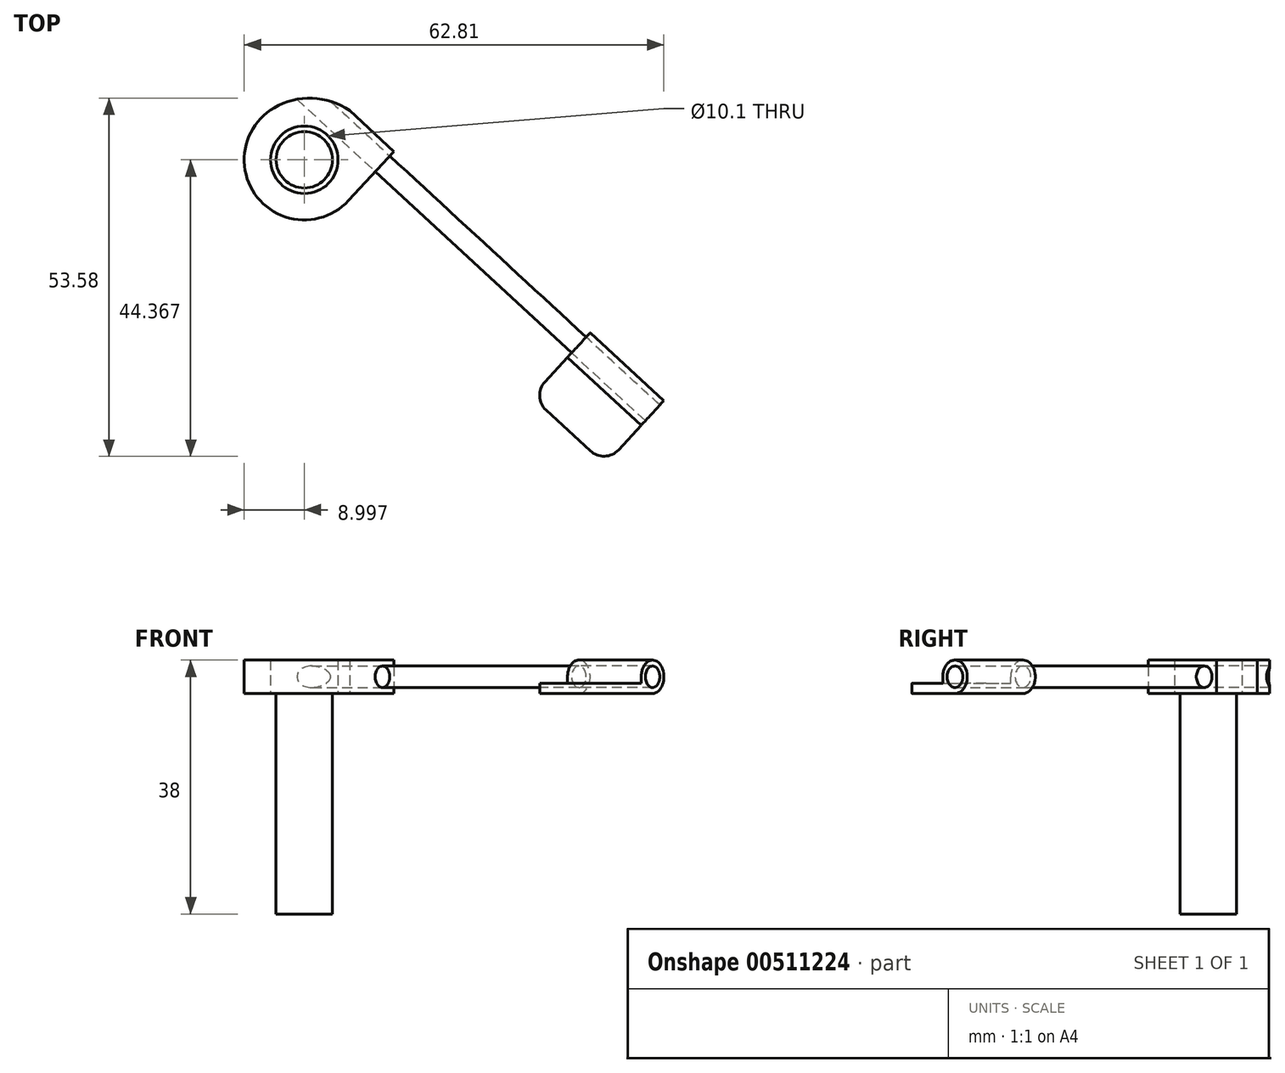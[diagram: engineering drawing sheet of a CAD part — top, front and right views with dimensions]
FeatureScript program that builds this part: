
annotation { "Feature Type Name" : "Feature", "Feature Type Description" : "" }
export const myFeature = defineFeature(function(context is Context, id is Id, definition is map)
    precondition{}
    {
        {
            var Q0;
            Q0=qCreatedBy(makeId("Top.planeOp"),FACE);
            var sketch = newSketch(context, id + "F0", { "sketchPlane" : qUnion([Q0])});
            skCircle(sketch, "E0", {"center": v(31.1, -55.05) * mm, "radius": 5 * mm});
            skCircle(sketch, "E1", {"center": v(31.1, -55.05) * mm, "radius": 4.22 * mm});
            skLineSegment(sketch, "E2", {"start": v(37.89, -47.7) * mm, "end": v(60.3, -68.38) * mm});
            skPoint(sketch, "E3.visualSharp", {"position": v(30.54, -40.92) * mm});
            skArc(sketch, "E3.filletArc", {"start": v(37.89, -47.7) * mm, "mid": v(30.7, -45.06) * mm, "end": v(23.76, -48.27) * mm});
            skArc(sketch, "E4", {"start": v(22.17, -56.11) * mm, "mid": v(31.47, -64.05) * mm, "end": v(40.1, -55.4) * mm});
            skLineSegment(sketch, "E5", {"start": v(16.9, -58.65) * mm, "end": v(19.92, -55.38) * mm});
            skLineSegment(sketch, "E6", {"start": v(42.29, -54.48) * mm, "end": v(58.96, -69.87) * mm});
            skPoint(sketch, "E7.endSnap0", {"position": v(14.35, -58.46) * mm});
            skPoint(sketch, "E8.orphan", {"position": v(57.46, -58.46) * mm});
            skArc(sketch, "E9.filletArc", {"start": v(22.17, -56.11) * mm, "mid": v(21.28, -55.03) * mm, "end": v(19.92, -55.38) * mm});
            skPoint(sketch, "E10.visualSharp", {"position": v(39.56, -51.97) * mm});
            skArc(sketch, "E10.filletArc", {"start": v(42.29, -54.48) * mm, "mid": v(40.9, -54.24) * mm, "end": v(40.1, -55.4) * mm});
            skSolve(sketch);
        }
        {
            var Q0;
            Q0=makeQuery(id+"F0.imprint","IMPRINT",FACE,{"disambiguationData":[TD([[makeQuery(id+"F0.imprint","IMPRINT",EDGE,{"derivedFrom":sQuery(id+"F0.wireOp",EDGE,"E1")}),1.0]])]});
            extrude(context, id + "F1", {"entities" : qUnion([Q0]), "depth" : 33 * mm, "offsetDistance" : 25 * mm});
        }
        {
            var Q0;
            Q0=makeQuery(id+"F0.imprint","IMPRINT",FACE,{"disambiguationData":[TD([[makeQuery(id+"F0.imprint","IMPRINT",EDGE,{"derivedFrom":sQuery(id+"F0.wireOp",EDGE,"E0")}),1.0]])]});
            extrude(context, id + "F2", {"entities" : qUnion([Q0]), "operationType" : NewBodyOperationType.REMOVE, "depth" : 5 * mm, "offsetDistance" : 25 * mm});
        }
        {
            var Q0;
            Q0=makeQuery(id+"F1.opExtrude","CAP_FACE",FACE,{"disambiguationData":[OSD([sQuery(id+"F0.wireOp",EDGE,"E1")])],"isStart":false});
            var sketch = newSketch(context, id + "F3", { "sketchPlane" : qUnion([Q0])});
            skCircle(sketch, "E11.0", {"center": v(31.1, -55.05) * mm, "radius": 5 * mm});
            skArc(sketch, "E11.1", {"start": v(22.17, -56.11) * mm, "mid": v(28.33, -63.61) * mm, "end": v(37.72, -61.16) * mm});
            skLineSegment(sketch, "E11.2", {"start": v(37.89, -47.7) * mm, "end": v(44.5, -53.8) * mm});
            skArc(sketch, "E12", {"start": v(26.6, -47.27) * mm, "mid": v(24.08, -60.68) * mm, "end": v(37.72, -61.16) * mm});
            skCircle(sketch, "E13", {"center": v(31.1, -55.05) * mm, "radius": 5.05 * mm});
            skArc(sketch, "E14", {"start": v(37.89, -47.7) * mm, "mid": v(32.3, -45.85) * mm, "end": v(26.6, -47.27) * mm});
            skLineSegment(sketch, "E15", {"start": v(37.72, -61.16) * mm, "end": v(43.15, -55.28) * mm});
            skLineSegment(sketch, "E16", {"start": v(43.15, -55.28) * mm, "end": v(44.5, -53.8) * mm});
            skSolve(sketch);
        }
        {
            var Q0;
            Q0=qSketchRegion(id+"F3",true);
            extrude(context, id + "F4", {"entities" : qUnion([Q0]), "depth" : 5 * mm, "offsetDistance" : 25 * mm});
        }
        {
            var Q0;
            Q0=makeQuery(id+"F4.opExtrude","SWEPT_FACE",FACE,{"disambiguationData":[OSD([sQuery(id+"F3.wireOp",EDGE,"E15"),sQuery(id+"F3.wireOp",EDGE,"E16")])]});
            var sketch = newSketch(context, id + "F5", { "sketchPlane" : qUnion([Q0])});
            skCircle(sketch, "E17", {"center": v(-11.86, 35.5) * mm, "radius": 1.6 * mm});
            skSolve(sketch);
        }
        {
            var Q0;
            Q0=qSketchRegion(id+"F5",true);
            extrude(context, id + "F6", {"entities" : qUnion([Q0]), "operationType" : NewBodyOperationType.REMOVE, "endBound" : BoundingType.THROUGH_ALL, "oppositeDirection" : true, "depth" : 25 * mm, "offsetDistance" : 25 * mm});
        }
        {
            var Q0;
            Q0 = qSketchRegion(id + "F5", true);
            extrude(context, id + "F7", {"entities" : qUnion([Q0]), "depth" : 40 * mm, "offsetDistance" : 25 * mm});
        }
        {
            var Q0;
            Q0=makeQuery(id+"F7.opExtrude","CAP_FACE",FACE,{"disambiguationData":[OSD([sQuery(id+"F5.wireOp",EDGE,"E17")])],"isStart":false});
            var sketch = newSketch(context, id + "F8", { "sketchPlane" : qUnion([Q0])});
            skLineSegment(sketch, "E18.0.0", {"start": v(-19.36, 33) * mm, "end": v(-11.86, 33) * mm});
            skLineSegment(sketch, "E18.0.1", {"start": v(-9.36, 35.5) * mm, "end": v(-9.36, 35.5) * mm});
            skLineSegment(sketch, "E18.0.2", {"start": v(-11.86, 38) * mm, "end": v(-11.86, 38) * mm});
            skLineSegment(sketch, "E18.0.3", {"start": v(-19.36, 38) * mm, "end": v(-19.36, 33) * mm});
            skLineSegment(sketch, "E19", {"start": v(-19.36, 33) * mm, "end": v(-22.36, 33) * mm});
            skLineSegment(sketch, "E20", {"start": v(-22.36, 33) * mm, "end": v(-22.36, 34.5) * mm});
            skLineSegment(sketch, "E21", {"start": v(-22.36, 34.5) * mm, "end": v(-14.36, 34.5) * mm});
            skLineSegment(sketch, "E22", {"start": v(-14.36, 34.5) * mm, "end": v(-14.36, 35.5) * mm});
            skPoint(sketch, "E23.newPointB", {"position": v(-19.36, 38) * mm});
            skArc(sketch, "E23.filletArc", {"start": v(-11.86, 38) * mm, "mid": v(-13.63, 37.27) * mm, "end": v(-14.36, 35.5) * mm});
            skPoint(sketch, "E24.visualSharp", {"position": v(-9.36, 38) * mm});
            skArc(sketch, "E24.filletArc", {"start": v(-9.36, 35.5) * mm, "mid": v(-10.1, 37.27) * mm, "end": v(-11.86, 38) * mm});
            skPoint(sketch, "E25.visualSharp", {"position": v(-9.36, 33) * mm});
            skArc(sketch, "E25.filletArc", {"start": v(-11.86, 33) * mm, "mid": v(-10.1, 33.73) * mm, "end": v(-9.36, 35.5) * mm});
            skSolve(sketch);
        }
        {
            var Q0;
            {var subQ0=sQuery(id+"F8.wireOp",EDGE,"E19");Q0=makeQuery(id+"F8.imprint","IMPRINT",FACE,{"disambiguationData":[TD([[makeQuery(id+"F8.imprint","IMPRINT",EDGE,{"derivedFrom":subQ0}),-1.0]])]});}
            var Q1;
            {var subQ2=sQuery(id+"F8.wireOp",EDGE,"E18.0.0");Q1=makeQuery(id+"F8.imprint","IMPRINT",FACE,{"disambiguationData":[TD([[makeQuery(id+"F8.imprint","IMPRINT",EDGE,{"derivedFrom":subQ2}),1.0]])]});}
            extrude(context, id + "F9", {"entities" : qUnion([Q0, Q1]), "depth" : 15 * mm, "offsetDistance" : 25 * mm});
        }
        {
            var Q0;
            Q0=makeQuery(id+"F9.opExtrude","CAP_EDGE",EDGE,{"disambiguationData":[OSD([sQuery(id+"F8.wireOp",EDGE,"E20")])],"isStart":false});
            var Q1;
            Q1=makeQuery(id+"F9.opExtrude","CAP_EDGE",EDGE,{"disambiguationData":[OSD([sQuery(id+"F8.wireOp",EDGE,"E20")])],"isStart":true});
            fillet(context, id + "F10", {"entities" : qUnion([Q0, Q1]), "radius" : 3 * mm, "tangentPropagation" : true, "allowEdgeOverflow" : false});
        }
    });
